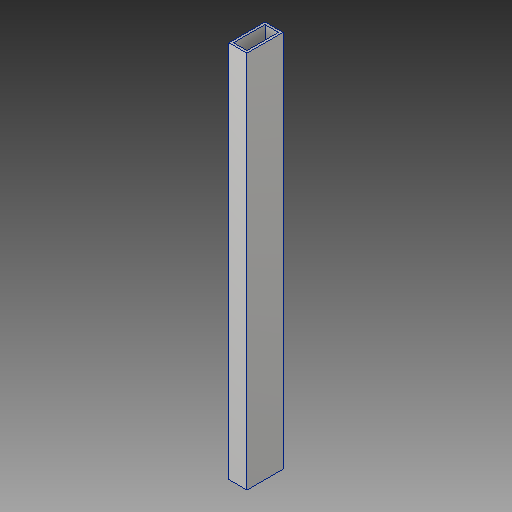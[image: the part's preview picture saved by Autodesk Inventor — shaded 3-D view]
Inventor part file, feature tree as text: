
AUTODESK INVENTOR PART (.ipt)
format: ipt  version: 2018 (Build 220112000, 112)  size: 101,888 bytes
history: native  units: in
note: dims shown in document units (in); Inventor stores cm internally (conversion verified against a paired STEP export)
features: extrude x1, sketch x1
ambient origin geometry x8: Origin, YZ Plane, XZ Plane, XY Plane, X Axis, Y Axis, Z Axis, Center Point
bodies: Solid1 (feature_tree)
feature tree (2):
  extrude  "Extrusion1"  Depth=2.0in
  sketch  "Sketch1"  dims[d0=1.0in d1=2.0in d2=0.125in d3=0.125in d4=0.125in d5=0.125in d6=21.0in d7=0.0in]
